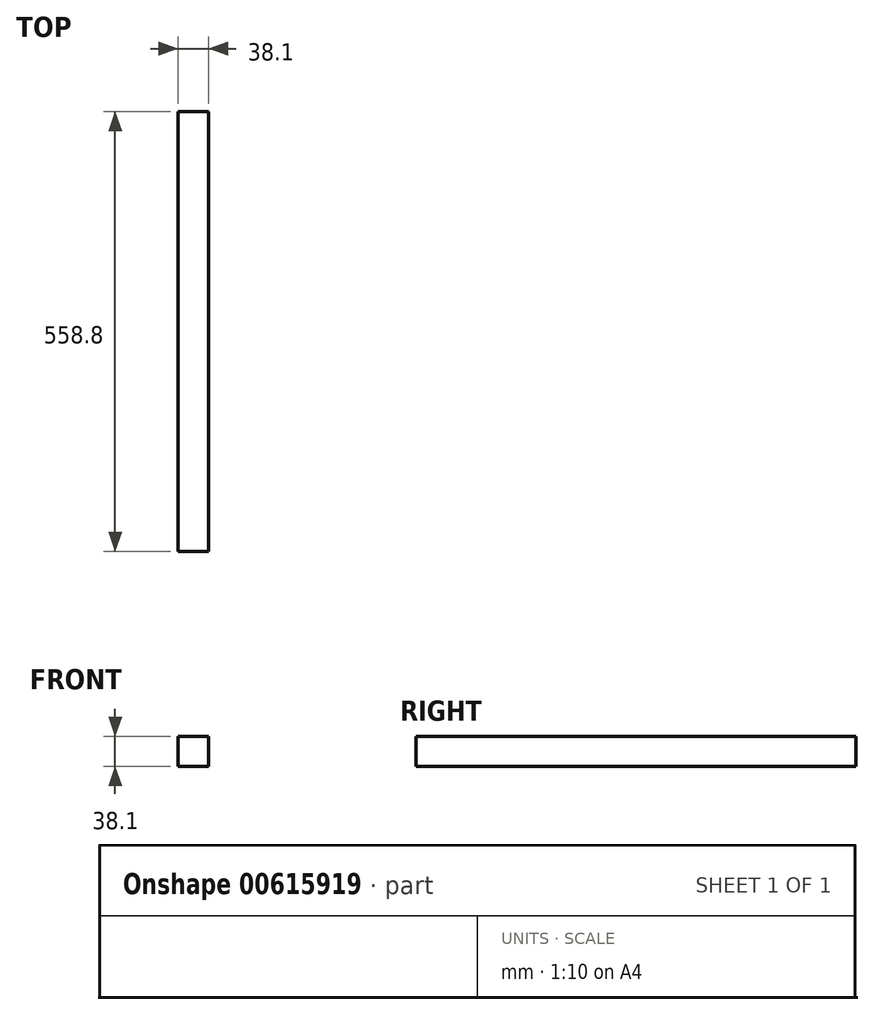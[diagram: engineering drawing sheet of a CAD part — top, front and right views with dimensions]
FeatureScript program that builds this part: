
annotation { "Feature Type Name" : "Feature", "Feature Type Description" : "" }
export const myFeature = defineFeature(function(context is Context, id is Id, definition is map)
    precondition{}
    {
        {
            var Q0;
            Q0=qCreatedBy(makeId("Front.planeOp"),FACE);
            var sketch = newSketch(context, id + "F0", { "sketchPlane" : qUnion([Q0])});
            skLineSegment(sketch, "E0.bottom", {"start": v(-19.05, 19.05) * mm, "end": v(19.05, 19.05) * mm});
            skLineSegment(sketch, "E0.top", {"start": v(-19.05, -19.05) * mm, "end": v(19.05, -19.05) * mm});
            skLineSegment(sketch, "E0.left", {"start": v(-19.05, 19.05) * mm, "end": v(-19.05, -19.05) * mm});
            skLineSegment(sketch, "E0.right", {"start": v(19.05, 19.05) * mm, "end": v(19.05, -19.05) * mm});
            skPoint(sketch, "E0.middle", {"position": v(0, 0) * mm});
            skSolve(sketch);
        }
        {
            var Q0;
            Q0 = qSketchRegion(id + "F0", true);
            extrude(context, id + "F1", {"entities" : qUnion([Q0]), "endBound" : BoundingType.SYMMETRIC, "depth" : 558.8 * mm, "offsetDistance" : 25.4 * mm});
        }
    });
